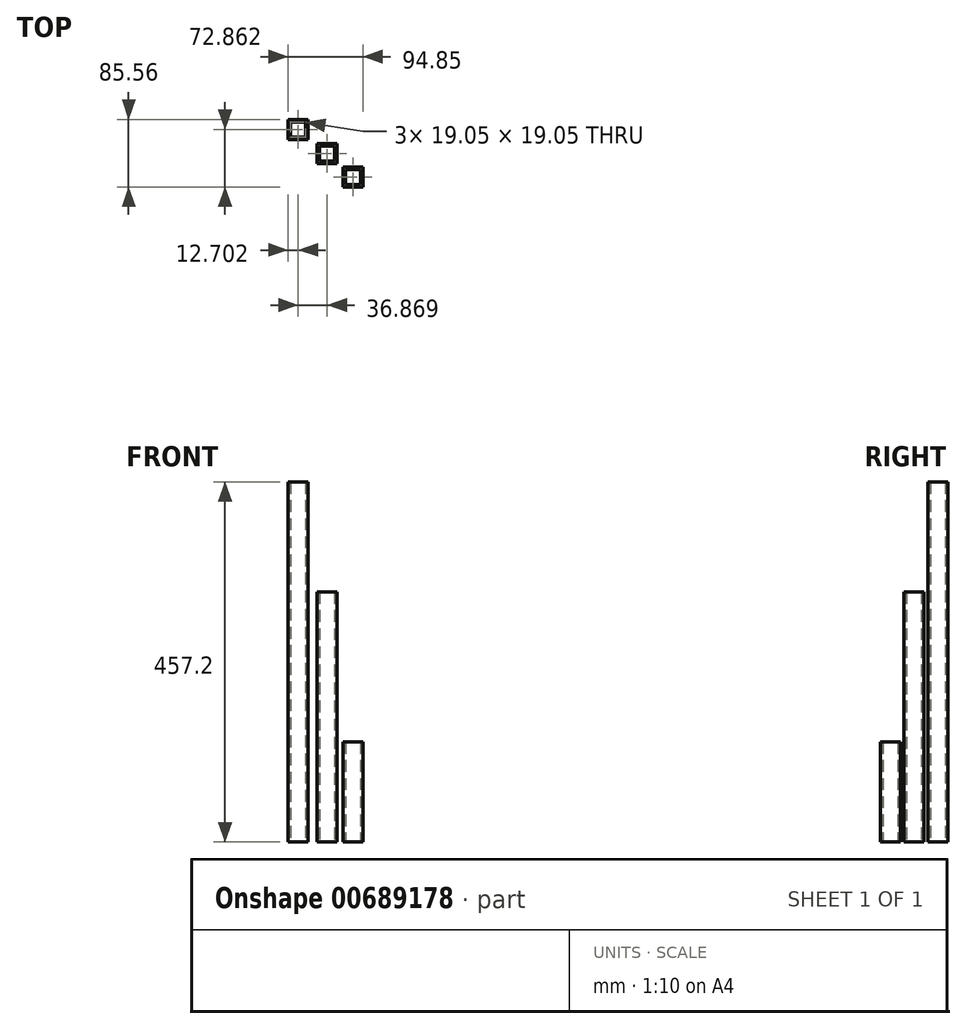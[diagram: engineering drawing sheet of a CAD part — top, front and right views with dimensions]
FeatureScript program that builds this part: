
annotation { "Feature Type Name" : "Feature", "Feature Type Description" : "" }
export const myFeature = defineFeature(function(context is Context, id is Id, definition is map)
    precondition{}
    {
        {
            var Q0;
            Q0=qCreatedBy(makeId("Top.planeOp"),FACE);
            var sketch = newSketch(context, id + "F0", { "sketchPlane" : qUnion([Q0])});
            skLineSegment(sketch, "E0.bottom", {"start": v(-78.39, 72.82) * mm, "end": v(-52.99, 72.82) * mm});
            skLineSegment(sketch, "E0.top", {"start": v(-78.39, 47.42) * mm, "end": v(-52.99, 47.42) * mm});
            skLineSegment(sketch, "E0.left", {"start": v(-78.39, 72.82) * mm, "end": v(-78.39, 47.42) * mm});
            skLineSegment(sketch, "E0.right", {"start": v(-52.99, 72.82) * mm, "end": v(-52.99, 47.42) * mm});
            skPoint(sketch, "E0.middle", {"position": v(-65.69, 60.12) * mm});
            skLineSegment(sketch, "E1.bottom", {"start": v(-75.21, 69.65) * mm, "end": v(-56.16, 69.65) * mm});
            skLineSegment(sketch, "E1.top", {"start": v(-75.21, 50.6) * mm, "end": v(-56.16, 50.6) * mm});
            skLineSegment(sketch, "E1.left", {"start": v(-75.21, 69.65) * mm, "end": v(-75.21, 50.6) * mm});
            skLineSegment(sketch, "E1.right", {"start": v(-56.16, 69.65) * mm, "end": v(-56.16, 50.6) * mm});
            skLineSegment(sketch, "E2.bottom", {"start": v(-41.52, 42.38) * mm, "end": v(-16.12, 42.38) * mm});
            skLineSegment(sketch, "E2.top", {"start": v(-41.52, 16.98) * mm, "end": v(-16.12, 16.98) * mm});
            skLineSegment(sketch, "E2.left", {"start": v(-41.52, 42.38) * mm, "end": v(-41.52, 16.98) * mm});
            skLineSegment(sketch, "E2.right", {"start": v(-16.12, 42.38) * mm, "end": v(-16.12, 16.98) * mm});
            skPoint(sketch, "E2.middle", {"position": v(-28.82, 29.68) * mm});
            skLineSegment(sketch, "E3.bottom", {"start": v(-38.34, 39.2) * mm, "end": v(-19.3, 39.2) * mm});
            skLineSegment(sketch, "E3.top", {"start": v(-38.34, 20.16) * mm, "end": v(-19.3, 20.16) * mm});
            skLineSegment(sketch, "E3.left", {"start": v(-38.34, 39.2) * mm, "end": v(-38.34, 20.16) * mm});
            skLineSegment(sketch, "E3.right", {"start": v(-19.3, 39.2) * mm, "end": v(-19.3, 20.16) * mm});
            skLineSegment(sketch, "E4.bottom", {"start": v(-8.94, 12.66) * mm, "end": v(16.46, 12.66) * mm});
            skLineSegment(sketch, "E4.top", {"start": v(-8.94, -12.74) * mm, "end": v(16.46, -12.74) * mm});
            skLineSegment(sketch, "E4.left", {"start": v(-8.94, 12.66) * mm, "end": v(-8.94, -12.74) * mm});
            skLineSegment(sketch, "E4.right", {"start": v(16.46, 12.66) * mm, "end": v(16.46, -12.74) * mm});
            skPoint(sketch, "E4.middle", {"position": v(3.76, -0.04) * mm});
            skLineSegment(sketch, "E5.bottom", {"start": v(-5.77, 9.49) * mm, "end": v(13.28, 9.49) * mm});
            skLineSegment(sketch, "E5.top", {"start": v(-5.77, -9.56) * mm, "end": v(13.28, -9.56) * mm});
            skLineSegment(sketch, "E5.left", {"start": v(-5.77, 9.49) * mm, "end": v(-5.77, -9.56) * mm});
            skLineSegment(sketch, "E5.right", {"start": v(13.28, 9.49) * mm, "end": v(13.28, -9.56) * mm});
            skSolve(sketch);
        }
        {
            var Q0;
            Q0=makeQuery(id+"F0.imprint","IMPRINT",FACE,{"disambiguationData":[TD([[makeQuery(id+"F0.imprint","IMPRINT",EDGE,{"derivedFrom":sQuery(id+"F0.wireOp",EDGE,"E0.bottom")}),-1.0]])]});
            extrude(context, id + "F1", {"entities" : qUnion([Q0]), "depth" : 457.2 * mm, "offsetDistance" : 25.4 * mm});
        }
        {
            var Q0;
            Q0=makeQuery(id+"F0.imprint","IMPRINT",FACE,{"disambiguationData":[TD([[makeQuery(id+"F0.imprint","IMPRINT",EDGE,{"derivedFrom":sQuery(id+"F0.wireOp",EDGE,"E2.bottom")}),-1.0]])]});
            extrude(context, id + "F2", {"entities" : qUnion([Q0]), "depth" : 317.5 * mm, "offsetDistance" : 25.4 * mm});
        }
        {
            var Q0;
            Q0=makeQuery(id+"F0.imprint","IMPRINT",FACE,{"disambiguationData":[TD([[makeQuery(id+"F0.imprint","IMPRINT",EDGE,{"derivedFrom":sQuery(id+"F0.wireOp",EDGE,"E4.bottom")}),-1.0]])]});
            extrude(context, id + "F3", {"entities" : qUnion([Q0]), "depth" : 127 * mm, "offsetDistance" : 25.4 * mm});
        }
    });
